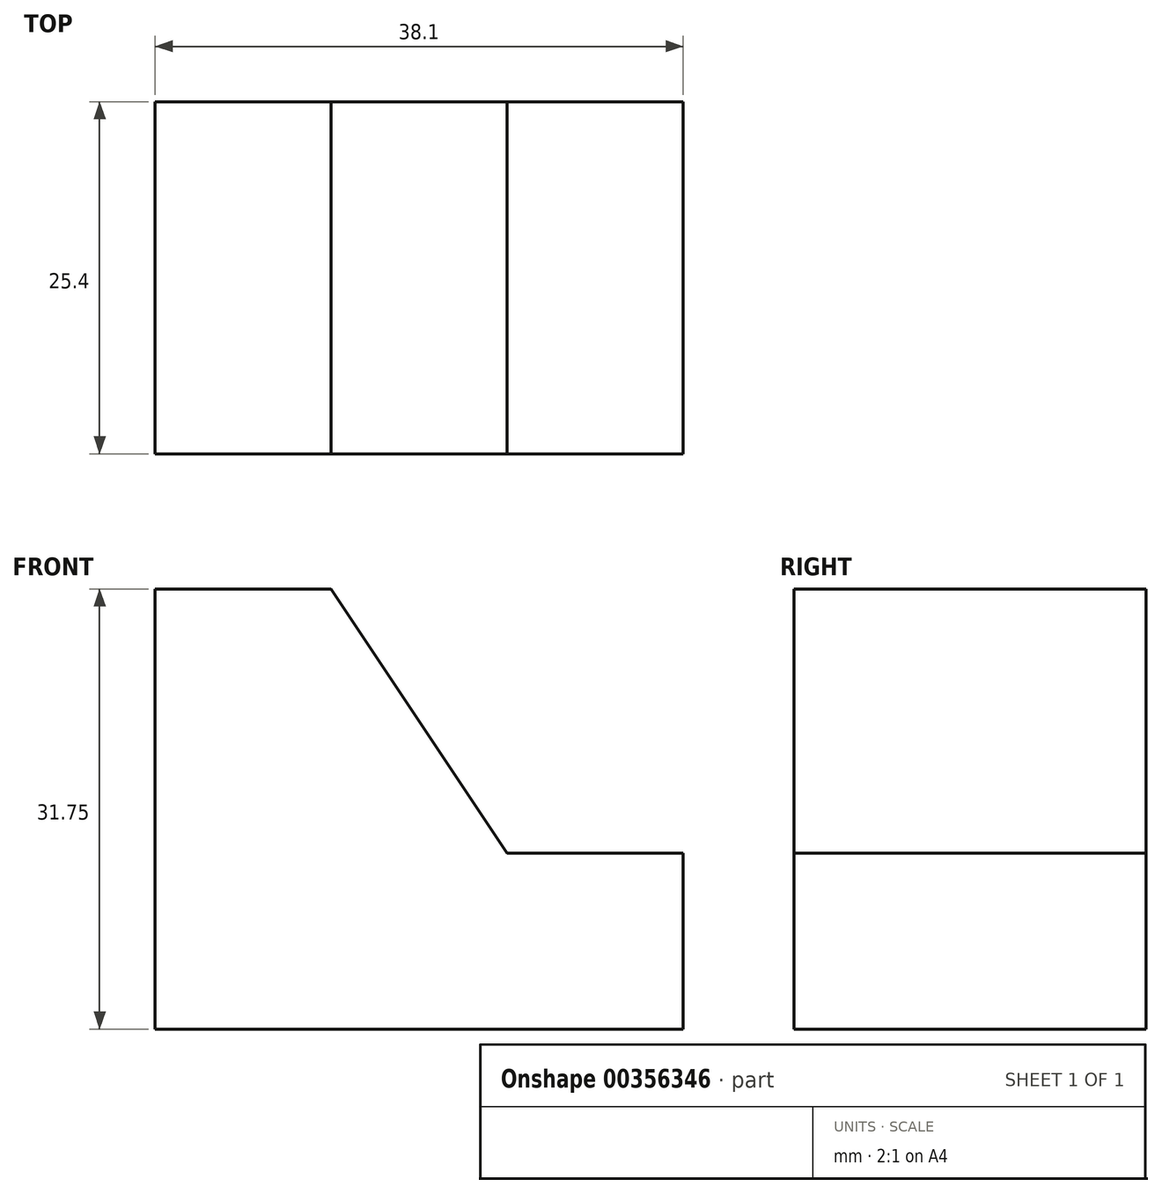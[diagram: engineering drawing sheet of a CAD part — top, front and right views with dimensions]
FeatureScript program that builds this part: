
annotation { "Feature Type Name" : "Feature", "Feature Type Description" : "" }
export const myFeature = defineFeature(function(context is Context, id is Id, definition is map)
    precondition{}
    {
        {
            var Q0;
            Q0=qCreatedBy(makeId("Front.planeOp"),FACE);
            var sketch = newSketch(context, id + "F0", { "sketchPlane" : qUnion([Q0])});
            skLineSegment(sketch, "E0", {"start": v(0, 0) * mm, "end": v(38.1, 0) * mm});
            skLineSegment(sketch, "E1", {"start": v(38.1, 0) * mm, "end": v(38.1, 12.7) * mm});
            skLineSegment(sketch, "E2", {"start": v(38.1, 12.7) * mm, "end": v(25.4, 12.7) * mm});
            skLineSegment(sketch, "E3", {"start": v(25.4, 12.7) * mm, "end": v(12.7, 31.75) * mm});
            skLineSegment(sketch, "E4", {"start": v(12.7, 31.75) * mm, "end": v(0, 31.75) * mm});
            skLineSegment(sketch, "E5", {"start": v(0, 31.75) * mm, "end": v(0, 0) * mm});
            skSolve(sketch);
        }
        {
            var Q0;
            Q0=makeQuery(id+"F0.imprint","IMPRINT",FACE,{"disambiguationData":[TD([[makeQuery(id+"F0.imprint","IMPRINT",EDGE,{"derivedFrom":sQuery(id+"F0.wireOp",EDGE,"E0")}),1.0]])]});
            extrude(context, id + "F1", {"entities" : qUnion([Q0]), "depth" : 25.4 * mm});
        }
    });
